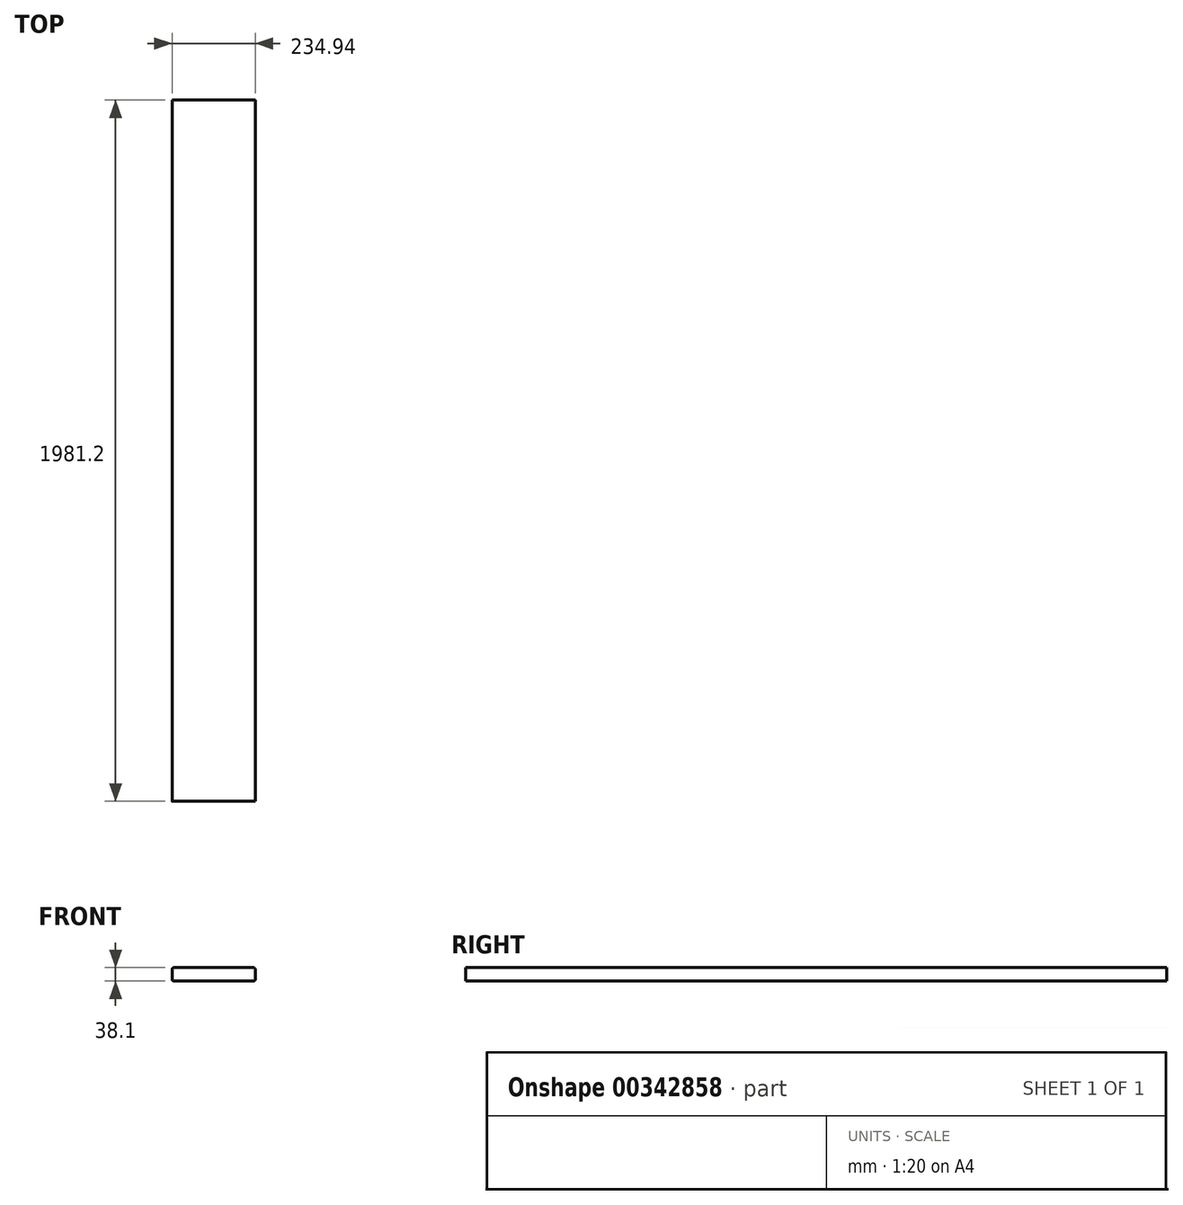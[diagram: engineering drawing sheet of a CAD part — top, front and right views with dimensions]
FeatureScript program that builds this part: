
annotation { "Feature Type Name" : "Feature", "Feature Type Description" : "" }
export const myFeature = defineFeature(function(context is Context, id is Id, definition is map)
    precondition{}
    {
        {
            var Q0;
            Q0=qCreatedBy(makeId("Front.planeOp"),FACE);
            var sketch = newSketch(context, id + "F0", { "sketchPlane" : qUnion([Q0])});
            skLineSegment(sketch, "E0.bottom", {"start": v(117.48, 19.05) * mm, "end": v(-117.48, 19.05) * mm});
            skLineSegment(sketch, "E0.top", {"start": v(117.48, -19.05) * mm, "end": v(-117.48, -19.05) * mm});
            skLineSegment(sketch, "E0.left", {"start": v(117.48, 19.05) * mm, "end": v(117.48, -19.05) * mm});
            skLineSegment(sketch, "E0.right", {"start": v(-117.48, 19.05) * mm, "end": v(-117.48, -19.05) * mm});
            skPoint(sketch, "E0.middle", {"position": v(0, 0) * mm});
            skSolve(sketch);
        }
        {
            var Q0;
            Q0=makeQuery(id+"F0.imprint","IMPRINT",FACE,{"disambiguationData":[TD([[makeQuery(id+"F0.imprint","IMPRINT",EDGE,{"derivedFrom":sQuery(id+"F0.wireOp",EDGE,"E0.bottom")}),1.0]])]});
            extrude(context, id + "F1", {"entities" : qUnion([Q0]), "endBound" : BoundingType.SYMMETRIC, "depth" : 1981.2 * mm});
        }
        {
            var Q0;
            Q0=makeQuery(id+"F1.opExtrude","SWEPT_EDGE",EDGE,{"disambiguationData":[OSD([sQuery(id+"F0.wireOp",EDGE,"E0.bottom"),sQuery(id+"F0.wireOp",EDGE,"E0.left")])]});
            var Q1;
            Q1=makeQuery(id+"F1.opExtrude","SWEPT_EDGE",EDGE,{"disambiguationData":[OSD([sQuery(id+"F0.wireOp",EDGE,"E0.top"),sQuery(id+"F0.wireOp",EDGE,"E0.left")])]});
            var Q2;
            Q2=makeQuery(id+"F1.opExtrude","SWEPT_EDGE",EDGE,{"disambiguationData":[OSD([sQuery(id+"F0.wireOp",EDGE,"E0.bottom"),sQuery(id+"F0.wireOp",EDGE,"E0.right")])]});
            var Q3;
            Q3=makeQuery(id+"F1.opExtrude","SWEPT_EDGE",EDGE,{"disambiguationData":[OSD([sQuery(id+"F0.wireOp",EDGE,"E0.top"),sQuery(id+"F0.wireOp",EDGE,"E0.right")])]});
            fillet(context, id + "F2", {"entities" : qUnion([Q0, Q1, Q2, Q3]), "radius" : 5.08 * mm, "tangentPropagation" : true, "allowEdgeOverflow" : false});
        }
    });
